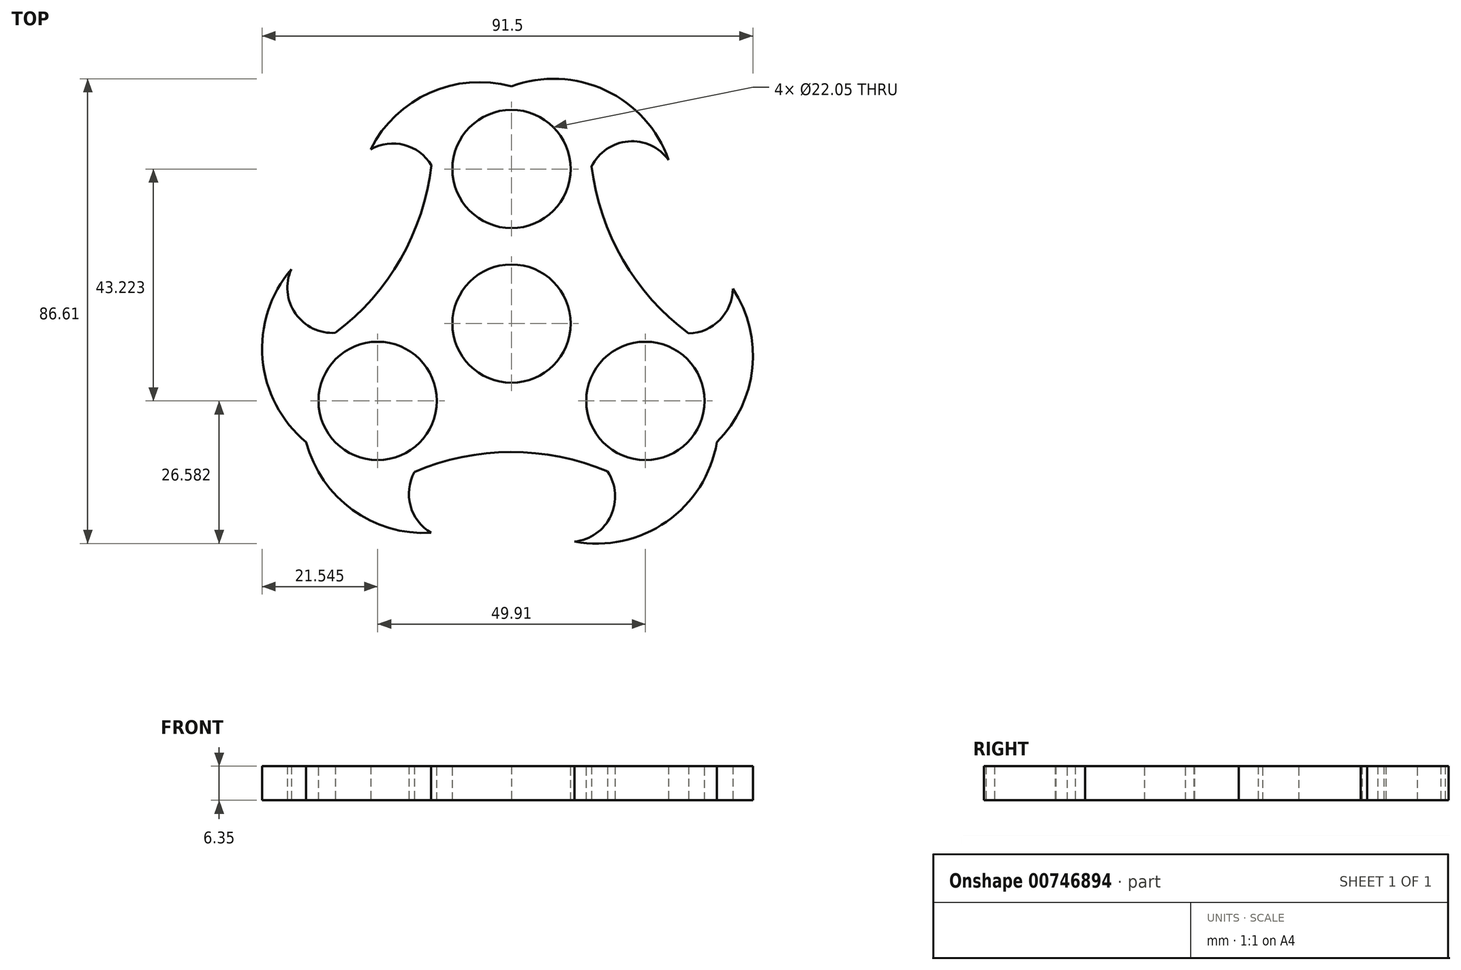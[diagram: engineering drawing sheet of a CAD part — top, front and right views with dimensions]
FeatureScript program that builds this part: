
annotation { "Feature Type Name" : "Feature", "Feature Type Description" : "" }
export const myFeature = defineFeature(function(context is Context, id is Id, definition is map)
    precondition{}
    {
        {
            var Q0;
            Q0=qCreatedBy(makeId("Top.planeOp"),FACE);
            var sketch = newSketch(context, id + "F0", { "sketchPlane" : qUnion([Q0])});
            skCircle(sketch, "E0", {"center": v(0, 0) * mm, "radius": 14.92 * mm});
            skCircle(sketch, "E1", {"center": v(0, 29.28) * mm, "radius": 14.92 * mm});
            skArc(sketch, "E2", {"start": v(0, 44.2) * mm, "mid": v(-15.23, 43.03) * mm, "end": v(-26.27, 32.47) * mm});
            skArc(sketch, "E3", {"start": v(-14.92, 29.5) * mm, "mid": v(-20, 33.3) * mm, "end": v(-26.27, 32.47) * mm});
            skArc(sketch, "E4", {"start": v(29.29, 30.49) * mm, "mid": v(17.52, 43.48) * mm, "end": v(0, 44.2) * mm});
            skArc(sketch, "E5", {"start": v(29.29, 30.49) * mm, "mid": v(21.76, 33.95) * mm, "end": v(14.92, 29.28) * mm});
            skCircle(sketch, "E6.1.0", {"center": v(-25.36, -14.64) * mm, "radius": 14.92 * mm});
            skArc(sketch, "E6.1.1", {"start": v(-38.28, -22.1) * mm, "mid": v(-29.65, -34.7) * mm, "end": v(-14.98, -38.98) * mm});
            skArc(sketch, "E6.1.2", {"start": v(-18.1, -27.68) * mm, "mid": v(-18.83, -33.96) * mm, "end": v(-14.98, -38.98) * mm});
            skArc(sketch, "E6.1.3", {"start": v(-41.05, 10.12) * mm, "mid": v(-46.41, -6.57) * mm, "end": v(-38.28, -22.1) * mm});
            skArc(sketch, "E6.1.4", {"start": v(-41.05, 10.12) * mm, "mid": v(-40.28, 1.87) * mm, "end": v(-32.82, -1.72) * mm});
            skCircle(sketch, "E6.2.0", {"center": v(25.36, -14.64) * mm, "radius": 14.92 * mm});
            skArc(sketch, "E6.2.1", {"start": v(38.28, -22.1) * mm, "mid": v(44.88, -8.32) * mm, "end": v(41.25, 6.52) * mm});
            skArc(sketch, "E6.2.2", {"start": v(33.02, -1.83) * mm, "mid": v(38.83, 0.67) * mm, "end": v(41.25, 6.52) * mm});
            skArc(sketch, "E6.2.3", {"start": v(11.76, -40.61) * mm, "mid": v(28.9, -36.91) * mm, "end": v(38.28, -22.1) * mm});
            skArc(sketch, "E6.2.4", {"start": v(11.76, -40.61) * mm, "mid": v(18.52, -35.82) * mm, "end": v(17.9, -27.56) * mm});
            skArc(sketch, "E7", {"start": v(14.92, 29.28) * mm, "mid": v(20.78, 11.87) * mm, "end": v(33.02, -1.83) * mm});
            skArc(sketch, "E8.1.0", {"start": v(-32.82, -1.72) * mm, "mid": v(-20.67, 12.06) * mm, "end": v(-14.92, 29.5) * mm});
            skArc(sketch, "E8.2.0", {"start": v(17.9, -27.56) * mm, "mid": v(-0.11, -23.93) * mm, "end": v(-18.1, -27.68) * mm});
            skSolve(sketch);
        }
        {
            var Q0;
            {var subQ5=sQuery(id+"F0.wireOp",EDGE,"E8.1.0");Q0=makeQuery(id+"F0.imprint","IMPRINT",FACE,{"disambiguationData":[TD([[makeQuery(id+"F0.imprint","IMPRINT",EDGE,{"derivedFrom":subQ5}),-1.0]])]});}
            var Q1;
            {var subQ0=sQuery(id+"F0.wireOp",EDGE,"E1");var subQ1=sQuery(id+"F0.wireOp",EDGE,"E0");var subQ2=makeQuery(id+"F0.imprint","INTERSECT",VERTEX,{"disambiguationData":[OD(0.0)],"derivedFrom":[subQ1,subQ0]});Q1=makeQuery(id+"F0.imprint","IMPRINT",FACE,{"disambiguationData":[TD([[makeQuery(id+"F0.imprint","IMPRINT",EDGE,{"disambiguationData":[TD([[subQ2,1.0]])],"derivedFrom":subQ1}),1.0]])]});}
            var Q2;
            {var subQ0=sQuery(id+"F0.wireOp",EDGE,"E6.2.1");Q2=makeQuery(id+"F0.imprint","IMPRINT",FACE,{"disambiguationData":[TD([[makeQuery(id+"F0.imprint","IMPRINT",EDGE,{"derivedFrom":subQ0}),1.0]])]});}
            var Q3;
            {var subQ0=sQuery(id+"F0.wireOp",EDGE,"E6.2.3");Q3=makeQuery(id+"F0.imprint","IMPRINT",FACE,{"disambiguationData":[TD([[makeQuery(id+"F0.imprint","IMPRINT",EDGE,{"derivedFrom":subQ0}),1.0]])]});}
            var Q4;
            {var subQ5=sQuery(id+"F0.wireOp",EDGE,"E7");Q4=makeQuery(id+"F0.imprint","IMPRINT",FACE,{"disambiguationData":[TD([[makeQuery(id+"F0.imprint","IMPRINT",EDGE,{"derivedFrom":subQ5}),-1.0]])]});}
            var Q5;
            {var subQ5=sQuery(id+"F0.wireOp",EDGE,"E8.2.0");Q5=makeQuery(id+"F0.imprint","IMPRINT",FACE,{"disambiguationData":[TD([[makeQuery(id+"F0.imprint","IMPRINT",EDGE,{"derivedFrom":subQ5}),-1.0]])]});}
            var Q6;
            {var subQ0=sQuery(id+"F0.wireOp",EDGE,"E1");var subQ2=sQuery(id+"F0.wireOp",EDGE,"E0");var subQ3=makeQuery(id+"F0.imprint","INTERSECT",VERTEX,{"disambiguationData":[OD(0.0)],"derivedFrom":[subQ2,subQ0]});Q6=makeQuery(id+"F0.imprint","IMPRINT",FACE,{"disambiguationData":[TD([[makeQuery(id+"F0.imprint","IMPRINT",EDGE,{"disambiguationData":[TD([[subQ3,1.0]])],"derivedFrom":subQ2}),-1.0]])]});}
            var Q7;
            {var subQ0=sQuery(id+"F0.wireOp",EDGE,"E1");var subQ1=sQuery(id+"F0.wireOp",EDGE,"E0");var subQ2=makeQuery(id+"F0.imprint","INTERSECT",VERTEX,{"disambiguationData":[OD(0.0)],"derivedFrom":[subQ1,subQ0]});Q7=makeQuery(id+"F0.imprint","IMPRINT",FACE,{"disambiguationData":[TD([[makeQuery(id+"F0.imprint","IMPRINT",EDGE,{"disambiguationData":[TD([[subQ2,-1.0]])],"derivedFrom":subQ1}),1.0]])]});}
            var Q8;
            {var subQ0=sQuery(id+"F0.wireOp",EDGE,"E6.1.0");var subQ4=sQuery(id+"F0.wireOp",EDGE,"E0");var subQ6=makeQuery(id+"F0.imprint","INTERSECT",VERTEX,{"disambiguationData":[OD(0.0)],"derivedFrom":[subQ4,subQ0]});Q8=makeQuery(id+"F0.imprint","IMPRINT",FACE,{"disambiguationData":[TD([[makeQuery(id+"F0.imprint","IMPRINT",EDGE,{"disambiguationData":[TD([[subQ6,-1.0]])],"derivedFrom":subQ4}),-1.0]])]});}
            var Q9;
            {var subQ0=sQuery(id+"F0.wireOp",EDGE,"E6.2.0");var subQ2=sQuery(id+"F0.wireOp",EDGE,"E0");var subQ4=makeQuery(id+"F0.imprint","INTERSECT",VERTEX,{"disambiguationData":[OD(0.0)],"derivedFrom":[subQ2,subQ0]});Q9=makeQuery(id+"F0.imprint","IMPRINT",FACE,{"disambiguationData":[TD([[makeQuery(id+"F0.imprint","IMPRINT",EDGE,{"disambiguationData":[TD([[subQ4,-1.0]])],"derivedFrom":subQ2}),-1.0]])]});}
            var Q10;
            {var subQ0=sQuery(id+"F0.wireOp",EDGE,"E4");Q10=makeQuery(id+"F0.imprint","IMPRINT",FACE,{"disambiguationData":[TD([[makeQuery(id+"F0.imprint","IMPRINT",EDGE,{"derivedFrom":subQ0}),1.0]])]});}
            var Q11;
            {var subQ0=sQuery(id+"F0.wireOp",EDGE,"E2");Q11=makeQuery(id+"F0.imprint","IMPRINT",FACE,{"disambiguationData":[TD([[makeQuery(id+"F0.imprint","IMPRINT",EDGE,{"derivedFrom":subQ0}),1.0]])]});}
            var Q12;
            {var subQ0=sQuery(id+"F0.wireOp",EDGE,"E6.1.3");Q12=makeQuery(id+"F0.imprint","IMPRINT",FACE,{"disambiguationData":[TD([[makeQuery(id+"F0.imprint","IMPRINT",EDGE,{"derivedFrom":subQ0}),1.0]])]});}
            var Q13;
            {var subQ0=sQuery(id+"F0.wireOp",EDGE,"E6.1.1");Q13=makeQuery(id+"F0.imprint","IMPRINT",FACE,{"disambiguationData":[TD([[makeQuery(id+"F0.imprint","IMPRINT",EDGE,{"derivedFrom":subQ0}),1.0]])]});}
            var Q14;
            {var subQ0=sQuery(id+"F0.wireOp",EDGE,"E6.1.0");var subQ1=sQuery(id+"F0.wireOp",EDGE,"E0");var subQ2=makeQuery(id+"F0.imprint","INTERSECT",VERTEX,{"disambiguationData":[OD(0.0)],"derivedFrom":[subQ1,subQ0]});Q14=makeQuery(id+"F0.imprint","IMPRINT",FACE,{"disambiguationData":[TD([[makeQuery(id+"F0.imprint","IMPRINT",EDGE,{"disambiguationData":[TD([[subQ2,-1.0]])],"derivedFrom":subQ1}),1.0]])]});}
            var Q15;
            {var subQ0=sQuery(id+"F0.wireOp",EDGE,"E6.2.0");var subQ1=sQuery(id+"F0.wireOp",EDGE,"E0");var subQ2=makeQuery(id+"F0.imprint","INTERSECT",VERTEX,{"disambiguationData":[OD(0.0)],"derivedFrom":[subQ1,subQ0]});Q15=makeQuery(id+"F0.imprint","IMPRINT",FACE,{"disambiguationData":[TD([[makeQuery(id+"F0.imprint","IMPRINT",EDGE,{"disambiguationData":[TD([[subQ2,-1.0]])],"derivedFrom":subQ1}),1.0]])]});}
            extrude(context, id + "F1", {"entities" : qUnion([Q0, Q1, Q2, Q3, Q4, Q5, Q6, Q7, Q8, Q9, Q10, Q11, Q12, Q13, Q14, Q15]), "depth" : 6.35 * mm, "offsetDistance" : 25.4 * mm});
        }
        {
            var Q0;
            Q0=makeQuery(id+"F1.opExtrude","CAP_FACE",FACE,{"disambiguationData":[OSD([sQuery(id+"F0.wireOp",EDGE,"E2"),sQuery(id+"F0.wireOp",EDGE,"E3"),sQuery(id+"F0.wireOp",EDGE,"E4"),sQuery(id+"F0.wireOp",EDGE,"E5"),sQuery(id+"F0.wireOp",EDGE,"E6.1.1"),sQuery(id+"F0.wireOp",EDGE,"E6.1.2"),sQuery(id+"F0.wireOp",EDGE,"E6.1.3"),sQuery(id+"F0.wireOp",EDGE,"E6.1.4"),sQuery(id+"F0.wireOp",EDGE,"E6.2.1"),sQuery(id+"F0.wireOp",EDGE,"E6.2.2"),sQuery(id+"F0.wireOp",EDGE,"E6.2.3"),sQuery(id+"F0.wireOp",EDGE,"E6.2.4"),sQuery(id+"F0.wireOp",EDGE,"E7"),sQuery(id+"F0.wireOp",EDGE,"E8.1.0"),sQuery(id+"F0.wireOp",EDGE,"E8.2.0")])],"isStart":false});
            var sketch = newSketch(context, id + "F2", { "sketchPlane" : qUnion([Q0])});
            skCircle(sketch, "E9", {"center": v(0, 0) * mm, "radius": 11.02 * mm});
            skCircle(sketch, "E10", {"center": v(0, 28.82) * mm, "radius": 11.02 * mm});
            skCircle(sketch, "E11.1.0", {"center": v(-24.95, -14.4) * mm, "radius": 11.02 * mm});
            skCircle(sketch, "E11.2.0", {"center": v(24.95, -14.4) * mm, "radius": 11.02 * mm});
            skSolve(sketch);
        }
        {
            var Q0;
            Q0 = qSketchRegion(id + "F2", true);
            extrude(context, id + "F3", {"entities" : qUnion([Q0]), "operationType" : NewBodyOperationType.REMOVE, "oppositeDirection" : true, "depth" : 25.4 * mm, "offsetDistance" : 25.4 * mm});
        }
    });
